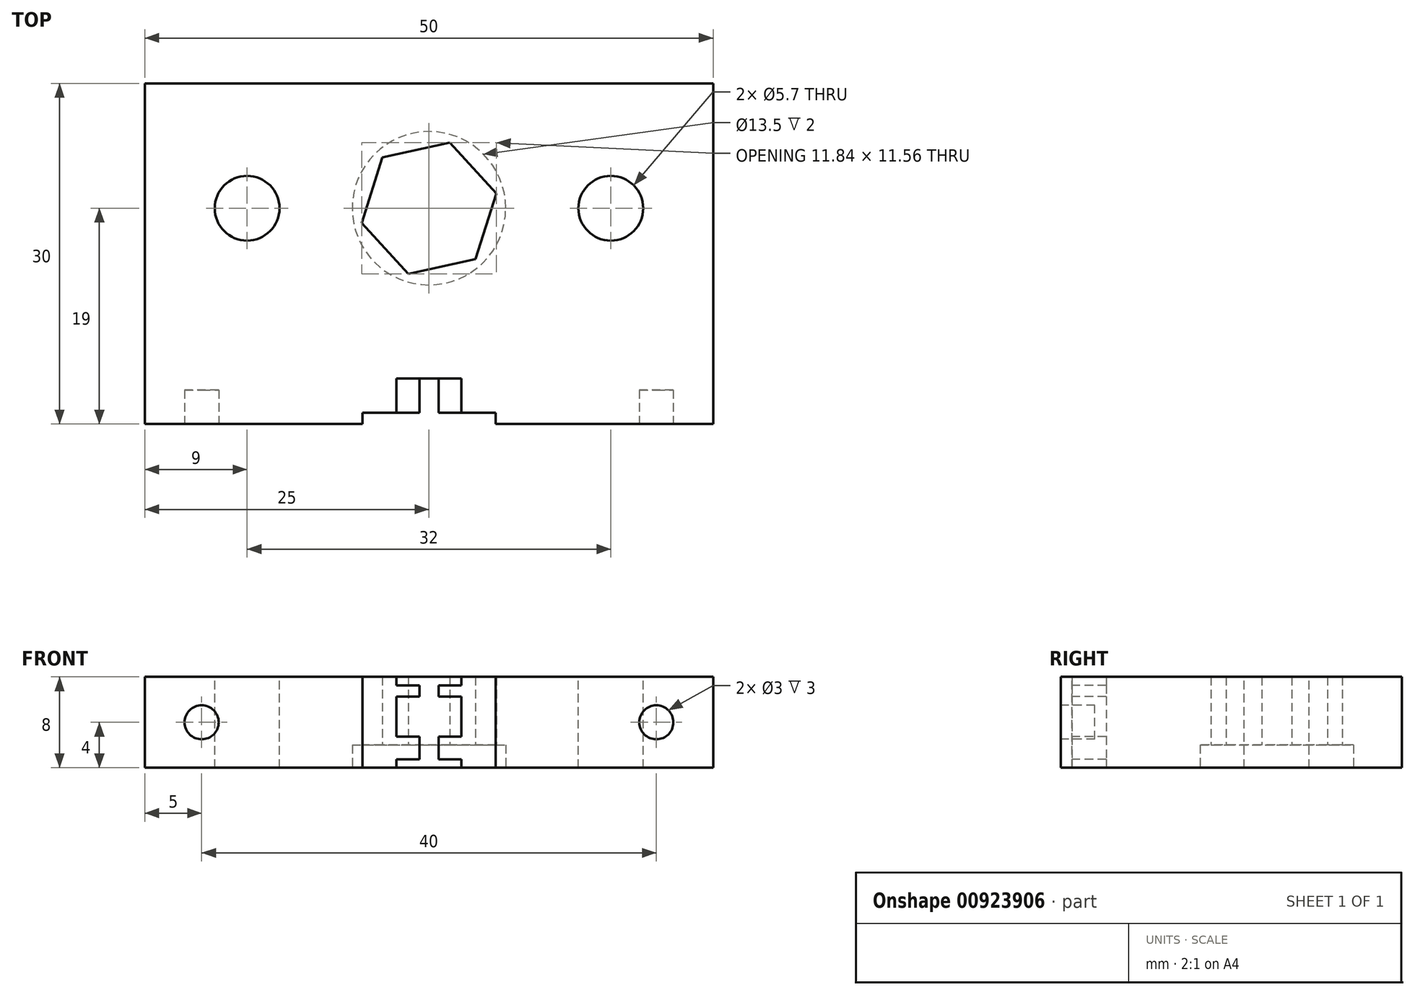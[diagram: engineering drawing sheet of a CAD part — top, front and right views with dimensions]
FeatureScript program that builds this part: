
annotation { "Feature Type Name" : "Feature", "Feature Type Description" : "" }
export const myFeature = defineFeature(function(context is Context, id is Id, definition is map)
    precondition{}
    {
        {
            var Q0;
            Q0=qCreatedBy(makeId("Top.planeOp"),FACE);
            var sketch = newSketch(context, id + "F0", { "sketchPlane" : qUnion([Q0])});
            skLineSegment(sketch, "E0.bottom", {"start": v(0, 0) * mm, "end": v(50, 0) * mm});
            skLineSegment(sketch, "E0.top", {"start": v(0, 30) * mm, "end": v(50, 30) * mm});
            skLineSegment(sketch, "E0.left", {"start": v(0, 0) * mm, "end": v(0, 30) * mm});
            skLineSegment(sketch, "E0.right", {"start": v(50, 0) * mm, "end": v(50, 30) * mm});
            skSolve(sketch);
        }
        {
            var Q0;
            Q0=makeQuery(id+"F0.imprint","IMPRINT",FACE,{"disambiguationData":[TD([[makeQuery(id+"F0.imprint","IMPRINT",EDGE,{"derivedFrom":sQuery(id+"F0.wireOp",EDGE,"E0.bottom")}),1.0]])]});
            extrude(context, id + "F1", {"entities" : qUnion([Q0]), "depth" : 8 * mm, "offsetDistance" : 25 * mm});
        }
        {
            var Q0;
            Q0=makeQuery(id+"F1.opExtrude","CAP_FACE",FACE,{"disambiguationData":[OSD([sQuery(id+"F0.wireOp",EDGE,"E0.bottom"),sQuery(id+"F0.wireOp",EDGE,"E0.top"),sQuery(id+"F0.wireOp",EDGE,"E0.left"),sQuery(id+"F0.wireOp",EDGE,"E0.right")])],"isStart":false});
            var sketch = newSketch(context, id + "F2", { "sketchPlane" : qUnion([Q0])});
            skCircle(sketch, "E1", {"center": v(41, 19) * mm, "radius": 2.85 * mm});
            skCircle(sketch, "E2", {"center": v(25, 19) * mm, "radius": 6.75 * mm});
            skCircle(sketch, "E3", {"center": v(9, 19) * mm, "radius": 2.85 * mm});
            skSolve(sketch);
        }
        {
            var Q0;
            Q0=makeQuery(id+"F2.imprint","IMPRINT",FACE,{"disambiguationData":[TD([[makeQuery(id+"F2.imprint","IMPRINT",EDGE,{"derivedFrom":sQuery(id+"F2.wireOp",EDGE,"E1")}),1.0]])]});
            var Q1;
            Q1=makeQuery(id+"F2.imprint","IMPRINT",FACE,{"disambiguationData":[TD([[makeQuery(id+"F2.imprint","IMPRINT",EDGE,{"derivedFrom":sQuery(id+"F2.wireOp",EDGE,"E3")}),1.0]])]});
            extrude(context, id + "F3", {"entities" : qUnion([Q0, Q1]), "operationType" : NewBodyOperationType.REMOVE, "oppositeDirection" : true, "depth" : 8 * mm, "offsetDistance" : 25 * mm});
        }
        {
            var Q0;
            {var subQ0=sQuery(id+"F0.wireOp",EDGE,"E0.right");var subQ3=sQuery(id+"F0.wireOp",EDGE,"E0.bottom");Q0=makeQuery(id+"F3.boolean.opBoolean","SPLIT",FACE,{"disambiguationData":[TD([makeQuery(id+"F1.opExtrude","SWEPT_FACE",FACE,{"disambiguationData":[OSD([subQ0])]})])],"derivedFrom":makeQuery(id+"F1.opExtrude","SWEPT_FACE",FACE,{"disambiguationData":[OSD([subQ3])]})});}
            var sketch = newSketch(context, id + "F4", { "sketchPlane" : qUnion([Q0])});
            skCircle(sketch, "E4", {"center": v(5, 4) * mm, "radius": 1.5 * mm});
            skCircle(sketch, "E5", {"center": v(45, 4) * mm, "radius": 1.5 * mm});
            skLineSegment(sketch, "E6", {"start": v(19.15, 0) * mm, "end": v(19.15, 8) * mm});
            skLineSegment(sketch, "E7", {"start": v(30.85, 0) * mm, "end": v(30.85, 8) * mm});
            skLineSegment(sketch, "E8", {"start": v(22.15, 8) * mm, "end": v(22.15, 7.25) * mm});
            skLineSegment(sketch, "E9", {"start": v(22.15, 7.25) * mm, "end": v(24.15, 7.25) * mm});
            skLineSegment(sketch, "E10", {"start": v(24.15, 7.25) * mm, "end": v(24.15, 6.25) * mm});
            skLineSegment(sketch, "E11", {"start": v(24.15, 6.25) * mm, "end": v(22.15, 6.25) * mm});
            skLineSegment(sketch, "E12", {"start": v(22.15, 6.25) * mm, "end": v(22.15, 2.75) * mm});
            skLineSegment(sketch, "E13", {"start": v(22.15, 2.75) * mm, "end": v(24.15, 2.75) * mm});
            skLineSegment(sketch, "E14", {"start": v(24.15, 2.75) * mm, "end": v(24.15, 0.75) * mm});
            skLineSegment(sketch, "E15", {"start": v(24.15, 0.75) * mm, "end": v(22.15, 0.75) * mm});
            skLineSegment(sketch, "E16", {"start": v(22.15, 0.75) * mm, "end": v(22.15, 0) * mm});
            skLineSegment(sketch, "E17", {"start": v(27.85, 8) * mm, "end": v(27.85, 7.25) * mm});
            skLineSegment(sketch, "E18", {"start": v(27.85, 7.25) * mm, "end": v(25.85, 7.25) * mm});
            skLineSegment(sketch, "E19", {"start": v(25.85, 7.25) * mm, "end": v(25.85, 6.25) * mm});
            skLineSegment(sketch, "E20", {"start": v(25.85, 6.25) * mm, "end": v(27.85, 6.25) * mm});
            skLineSegment(sketch, "E21", {"start": v(27.85, 6.25) * mm, "end": v(27.85, 2.75) * mm});
            skLineSegment(sketch, "E22", {"start": v(27.85, 2.75) * mm, "end": v(25.85, 2.75) * mm});
            skLineSegment(sketch, "E23", {"start": v(25.85, 2.75) * mm, "end": v(25.85, 0.75) * mm});
            skLineSegment(sketch, "E24", {"start": v(25.85, 0.75) * mm, "end": v(27.85, 0.75) * mm});
            skLineSegment(sketch, "E25", {"start": v(27.85, 0.75) * mm, "end": v(27.85, 0) * mm});
            skSolve(sketch);
        }
        {
            var Q0;
            Q0=makeQuery(id+"F4.imprint","IMPRINT",FACE,{"disambiguationData":[TD([[makeQuery(id+"F4.imprint","IMPRINT",EDGE,{"derivedFrom":sQuery(id+"F4.wireOp",EDGE,"E4")}),1.0]])]});
            var Q1;
            Q1=makeQuery(id+"F4.imprint","IMPRINT",FACE,{"disambiguationData":[TD([[makeQuery(id+"F4.imprint","IMPRINT",EDGE,{"derivedFrom":sQuery(id+"F4.wireOp",EDGE,"E5")}),1.0]])]});
            extrude(context, id + "F5", {"entities" : qUnion([Q0, Q1]), "operationType" : NewBodyOperationType.REMOVE, "oppositeDirection" : true, "depth" : 3 * mm, "offsetDistance" : 25 * mm});
        }
        {
            var Q0;
            {var subQ2=sQuery(id+"F4.wireOp",EDGE,"E8");Q0=makeQuery(id+"F4.imprint","IMPRINT",FACE,{"disambiguationData":[TD([[makeQuery(id+"F4.imprint","IMPRINT",EDGE,{"derivedFrom":subQ2}),1.0]])]});}
            extrude(context, id + "F6", {"entities" : qUnion([Q0]), "operationType" : NewBodyOperationType.REMOVE, "oppositeDirection" : true, "depth" : 4 * mm, "offsetDistance" : 25 * mm});
        }
        {
            var Q0;
            {var subQ1=sQuery(id+"F4.wireOp",EDGE,"E6");Q0=makeQuery(id+"F4.imprint","IMPRINT",FACE,{"disambiguationData":[TD([[makeQuery(id+"F4.imprint","IMPRINT",EDGE,{"derivedFrom":subQ1}),-1.0]])]});}
            var Q1;
            {var subQ2=sQuery(id+"F4.wireOp",EDGE,"E7");Q1=makeQuery(id+"F4.imprint","IMPRINT",FACE,{"disambiguationData":[TD([[makeQuery(id+"F4.imprint","IMPRINT",EDGE,{"derivedFrom":subQ2}),1.0]])]});}
            extrude(context, id + "F7", {"entities" : qUnion([Q0, Q1]), "operationType" : NewBodyOperationType.REMOVE, "oppositeDirection" : true, "depth" : 1 * mm, "offsetDistance" : 25 * mm});
        }
        {
            var Q0;
            Q0=makeQuery(id+"F1.opExtrude","CAP_FACE",FACE,{"disambiguationData":[OSD([sQuery(id+"F0.wireOp",EDGE,"E0.bottom"),sQuery(id+"F0.wireOp",EDGE,"E0.top"),sQuery(id+"F0.wireOp",EDGE,"E0.left"),sQuery(id+"F0.wireOp",EDGE,"E0.right")])],"isStart":true});
            var sketch = newSketch(context, id + "F8", { "sketchPlane" : qUnion([Q0])});
            skCircle(sketch, "E26", {"center": v(25, -19) * mm, "radius": 6.75 * mm});
            skSolve(sketch);
        }
        {
            var Q0;
            Q0=makeQuery(id+"F8.imprint","IMPRINT",FACE,{"disambiguationData":[TD([[makeQuery(id+"F8.imprint","IMPRINT",EDGE,{"derivedFrom":sQuery(id+"F8.wireOp",EDGE,"E26")}),1.0]])]});
            extrude(context, id + "F9", {"entities" : qUnion([Q0]), "operationType" : NewBodyOperationType.REMOVE, "oppositeDirection" : true, "depth" : 2 * mm, "offsetDistance" : 25 * mm});
        }
        {
            var Q0;
            Q0=makeQuery(id+"F9.boolean.opBoolean","COPY",FACE,{"derivedFrom":makeQuery(id+"F9.opExtrude","CAP_FACE",FACE,{"disambiguationData":[OSD([sQuery(id+"F8.wireOp",EDGE,"E26")])],"isStart":false})});
            var sketch = newSketch(context, id + "F10", { "sketchPlane" : qUnion([Q0])});
            skCircle(sketch, "E27.cCircle", {"center": v(25, -19) * mm, "radius": 5.25 * mm, "construction": true});
            skLineSegment(sketch, "E27.0", {"start": v(29.1, -14.53) * mm, "end": v(30.92, -20.31) * mm});
            skLineSegment(sketch, "E27.1", {"start": v(30.92, -20.31) * mm, "end": v(26.82, -24.78) * mm});
            skLineSegment(sketch, "E27.2", {"start": v(26.82, -24.78) * mm, "end": v(20.9, -23.47) * mm});
            skLineSegment(sketch, "E27.3", {"start": v(20.9, -23.47) * mm, "end": v(19.08, -17.69) * mm});
            skLineSegment(sketch, "E27.4", {"start": v(19.08, -17.69) * mm, "end": v(23.18, -13.22) * mm});
            skLineSegment(sketch, "E27.5", {"start": v(23.18, -13.22) * mm, "end": v(29.1, -14.53) * mm});
            skPoint(sketch, "E27.0.midPoint", {"position": v(30, -17.42) * mm});
            skSolve(sketch);
        }
        {
            var Q0;
            Q0=makeQuery(id+"F10.imprint","IMPRINT",FACE,{"disambiguationData":[TD([[makeQuery(id+"F10.imprint","IMPRINT",EDGE,{"derivedFrom":sQuery(id+"F10.wireOp",EDGE,"E27.0")}),-1.0]])]});
            extrude(context, id + "F11", {"entities" : qUnion([Q0]), "operationType" : NewBodyOperationType.REMOVE, "oppositeDirection" : true, "depth" : 6 * mm, "offsetDistance" : 25 * mm});
        }
    });
